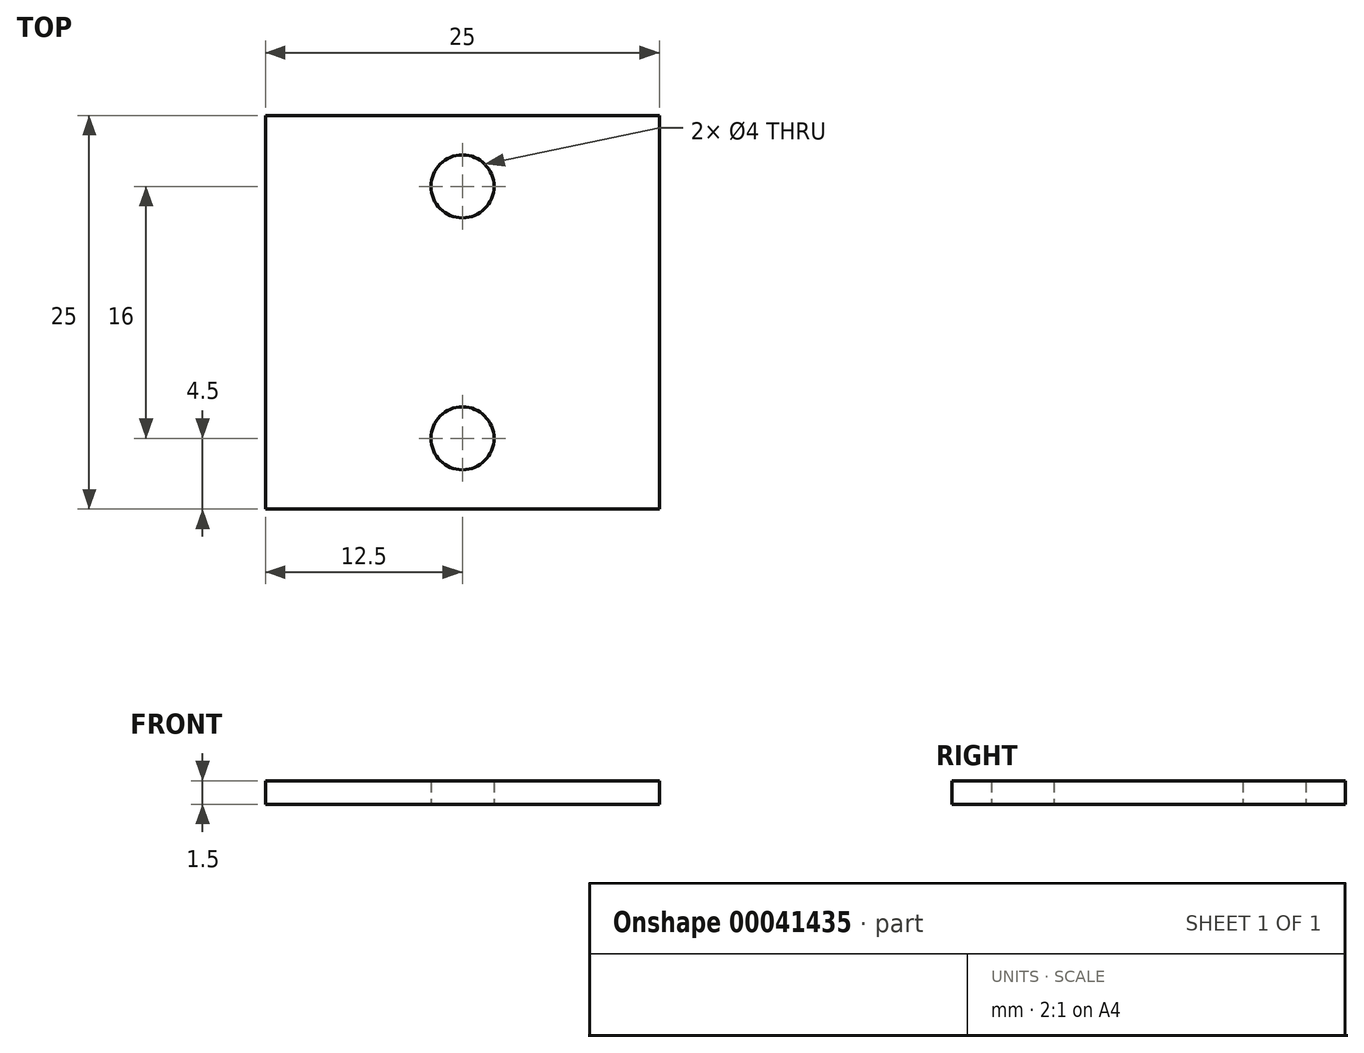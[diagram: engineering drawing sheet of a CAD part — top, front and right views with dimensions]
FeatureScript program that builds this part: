
annotation { "Feature Type Name" : "Feature", "Feature Type Description" : "" }
export const myFeature = defineFeature(function(context is Context, id is Id, definition is map)
    precondition{}
    {
        {
            var Q0;
            Q0=qCreatedBy(makeId("Top.planeOp"),FACE);
            var sketch = newSketch(context, id + "F0", { "sketchPlane" : qUnion([Q0])});
            skLineSegment(sketch, "E0.bottom", {"start": v(0, 0) * mm, "end": v(25, 0) * mm});
            skLineSegment(sketch, "E0.top", {"start": v(0, -25) * mm, "end": v(25, -25) * mm});
            skLineSegment(sketch, "E0.left", {"start": v(0, 0) * mm, "end": v(0, -25) * mm});
            skLineSegment(sketch, "E0.right", {"start": v(25, 0) * mm, "end": v(25, -25) * mm});
            skLineSegment(sketch, "E1", {"start": v(12.5, -25) * mm, "end": v(12.5, 0) * mm, "construction": true});
            skLineSegment(sketch, "E2", {"start": v(0, -12.5) * mm, "end": v(25, -12.5) * mm, "construction": true});
            skLineSegment(sketch, "E3.0", {"start": v(0, -20.5) * mm, "end": v(25, -20.5) * mm, "construction": true});
            skLineSegment(sketch, "E4.0", {"start": v(0, -4.5) * mm, "end": v(25, -4.5) * mm, "construction": true});
            skCircle(sketch, "E5", {"center": v(12.5, -4.5) * mm, "radius": 2 * mm});
            skCircle(sketch, "E6.MirrorC", {"center": v(12.5, -20.5) * mm, "radius": 2 * mm});
            skSolve(sketch);
        }
        {
            var Q0;
            Q0=makeQuery(id+"F0.imprint","IMPRINT",FACE,{"disambiguationData":[TD([[makeQuery(id+"F0.imprint","IMPRINT",EDGE,{"derivedFrom":sQuery(id+"F0.wireOp",EDGE,"E0.bottom")}),-1.0]])]});
            extrude(context, id + "F1", {"entities" : qUnion([Q0]), "depth" : 1.5 * mm});
        }
    });
